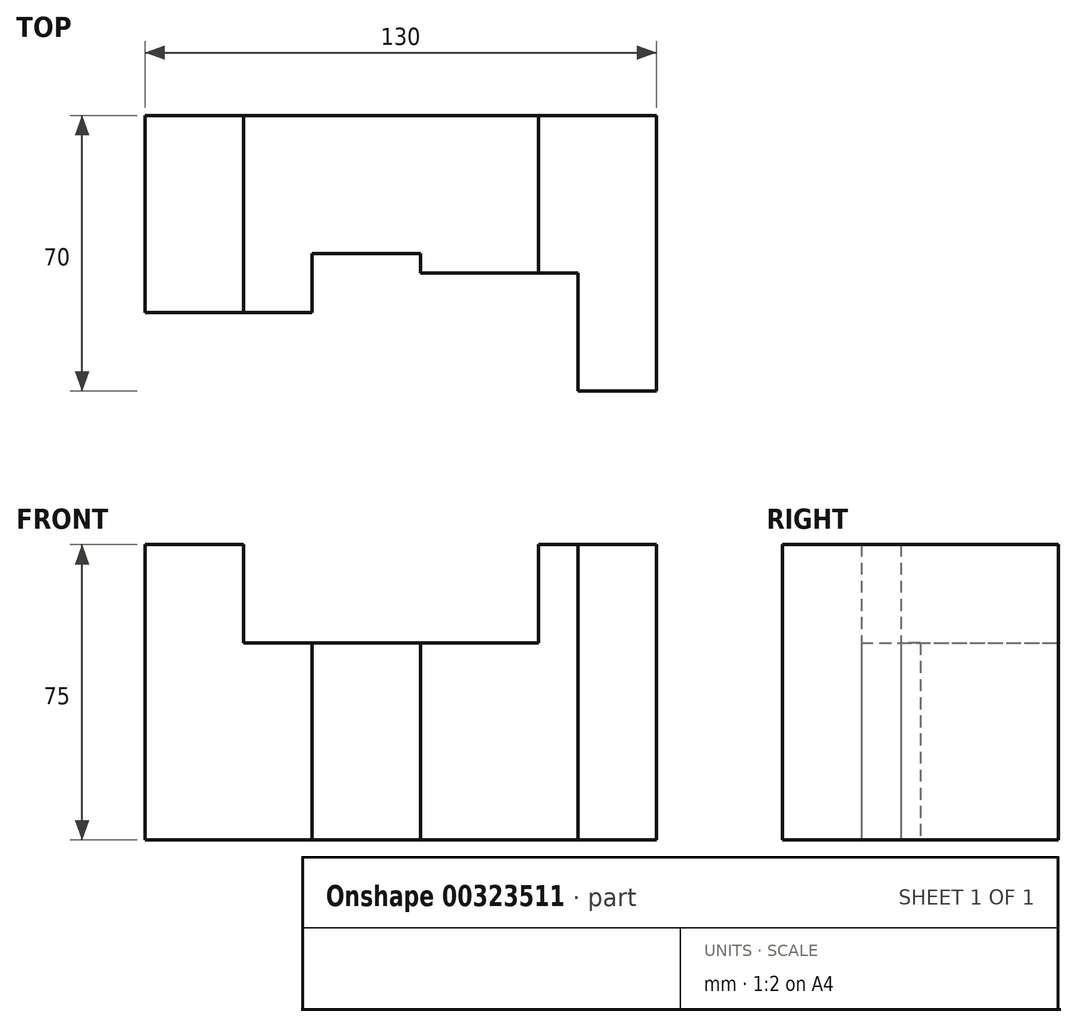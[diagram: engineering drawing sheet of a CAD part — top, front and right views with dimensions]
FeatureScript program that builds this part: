
annotation { "Feature Type Name" : "Feature", "Feature Type Description" : "" }
export const myFeature = defineFeature(function(context is Context, id is Id, definition is map)
    precondition{}
    {
        {
            var Q0;
            Q0=qCreatedBy(makeId("Top.planeOp"),FACE);
            var sketch = newSketch(context, id + "F0", { "sketchPlane" : qUnion([Q0])});
            skLineSegment(sketch, "E0", {"start": v(0, 50) * mm, "end": v(25, 50) * mm});
            skLineSegment(sketch, "E1", {"start": v(25, 50) * mm, "end": v(25, 0) * mm});
            skLineSegment(sketch, "E2", {"start": v(25, 0) * mm, "end": v(0, 0) * mm});
            skLineSegment(sketch, "E3", {"start": v(0, 50) * mm, "end": v(0, 0) * mm});
            skSolve(sketch);
        }
        {
            var Q0;
            Q0 = qSketchRegion(id + "F0", true);
            extrude(context, id + "F1", {"entities" : qUnion([Q0]), "depth" : 75 * mm});
        }
        {
            var Q0;
            Q0=qCreatedBy(makeId("Top.planeOp"),FACE);
            var sketch = newSketch(context, id + "F2", { "sketchPlane" : qUnion([Q0])});
            skLineSegment(sketch, "E4", {"start": v(25, 0) * mm, "end": v(42.5, 0) * mm});
            skLineSegment(sketch, "E5", {"start": v(42.5, 0) * mm, "end": v(42.5, 15) * mm});
            skLineSegment(sketch, "E6", {"start": v(42.5, 15) * mm, "end": v(70, 15) * mm});
            skLineSegment(sketch, "E7", {"start": v(70, 15) * mm, "end": v(70, 10) * mm});
            skLineSegment(sketch, "E8", {"start": v(70, 10) * mm, "end": v(100, 10) * mm});
            skLineSegment(sketch, "E9", {"start": v(100, 10) * mm, "end": v(100, 40) * mm});
            skLineSegment(sketch, "E10", {"start": v(90, 50) * mm, "end": v(25, 50) * mm});
            skLineSegment(sketch, "E11", {"start": v(25, 0) * mm, "end": v(25, 50) * mm});
            skLineSegment(sketch, "E12", {"start": v(100, 40) * mm, "end": v(100, 50) * mm});
            skLineSegment(sketch, "E13", {"start": v(100, 50) * mm, "end": v(90, 50) * mm});
            skSolve(sketch);
        }
        {
            var Q0;
            Q0 = qSketchRegion(id + "F2", true);
            extrude(context, id + "F3", {"entities" : qUnion([Q0]), "operationType" : NewBodyOperationType.ADD, "depth" : 50 * mm});
        }
        {
            var Q0;
            Q0=makeQuery(id+"F3.boolean.opBoolean","MERGE",FACE,{"derivedFrom":[makeQuery(id+"F1.opExtrude","CAP_FACE",FACE,{"disambiguationData":[OSD([sQuery(id+"F0.wireOp",EDGE,"E0"),sQuery(id+"F0.wireOp",EDGE,"E1"),sQuery(id+"F0.wireOp",EDGE,"E2"),sQuery(id+"F0.wireOp",EDGE,"E3")])],"isStart":true}),makeQuery(id+"F3.opExtrude","CAP_FACE",FACE,{"disambiguationData":[OSD([sQuery(id+"F2.wireOp",EDGE,"E4"),sQuery(id+"F2.wireOp",EDGE,"E5"),sQuery(id+"F2.wireOp",EDGE,"E6"),sQuery(id+"F2.wireOp",EDGE,"E7"),sQuery(id+"F2.wireOp",EDGE,"E8"),sQuery(id+"F2.wireOp",EDGE,"E9"),sQuery(id+"F2.wireOp",EDGE,"A4biukky-5KVo-xXr9-DDjf-YokITq7f7Mpo"),sQuery(id+"F2.wireOp",EDGE,"CXbMiuoN-gvWE-pZ3l-1ATw-nRsuDFMijNGI"),sQuery(id+"F2.wireOp",EDGE,"E10"),sQuery(id+"F2.wireOp",EDGE,"E11")])],"isStart":true})]});
            var sketch = newSketch(context, id + "F4", { "sketchPlane" : qUnion([Q0])});
            skLineSegment(sketch, "E14", {"start": v(100, -10) * mm, "end": v(110, -10) * mm});
            skLineSegment(sketch, "E15", {"start": v(110, -10) * mm, "end": v(110, 20) * mm});
            skLineSegment(sketch, "E16", {"start": v(110, 20) * mm, "end": v(130, 20) * mm});
            skLineSegment(sketch, "E17", {"start": v(130, 20) * mm, "end": v(130, -50) * mm});
            skLineSegment(sketch, "E18", {"start": v(130, -50) * mm, "end": v(100, -50) * mm});
            skLineSegment(sketch, "E19", {"start": v(100, -50) * mm, "end": v(100, -10) * mm});
            skSolve(sketch);
        }
        {
            var Q0;
            Q0 = qSketchRegion(id + "F4", true);
            extrude(context, id + "F5", {"entities" : qUnion([Q0]), "operationType" : NewBodyOperationType.ADD, "oppositeDirection" : true, "depth" : 75 * mm});
        }
    });
